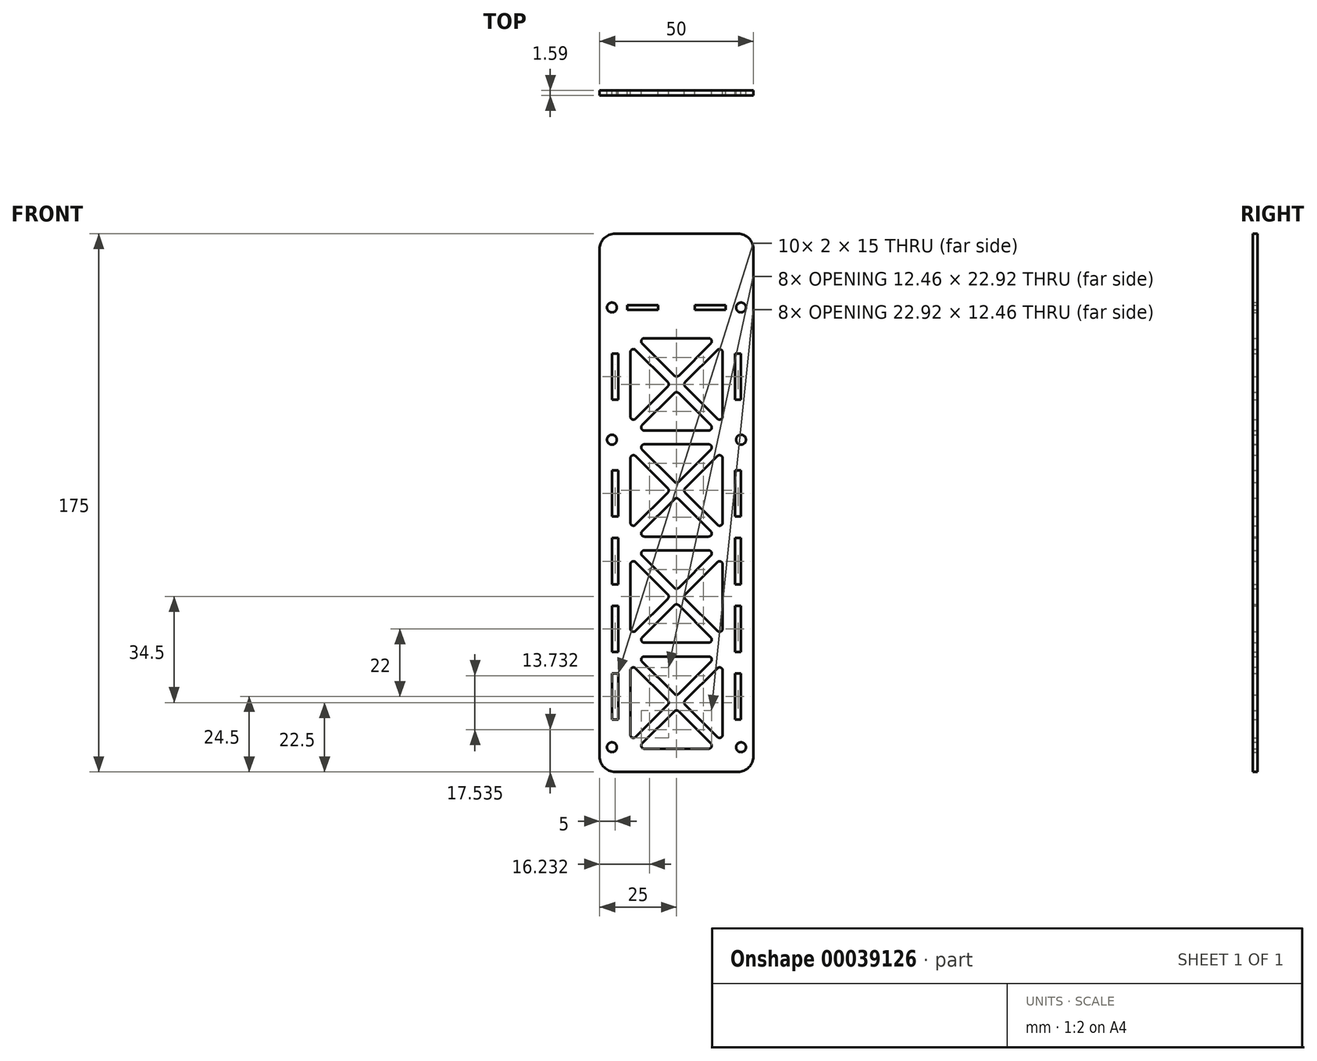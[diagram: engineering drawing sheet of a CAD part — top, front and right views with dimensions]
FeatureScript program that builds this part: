
annotation { "Feature Type Name" : "Feature", "Feature Type Description" : "" }
export const myFeature = defineFeature(function(context is Context, id is Id, definition is map)
    precondition{}
    {
        {
            var Q0;
            Q0=qCreatedBy(makeId("Front.planeOp"),FACE);
            var sketch = newSketch(context, id + "F0", { "sketchPlane" : qUnion([Q0])});
            skArc(sketch, "E0", {"start": v(15, -54.54) * mm, "mid": v(14.38, -53.61) * mm, "end": v(13.3, -53.83) * mm});
            skLineSegment(sketch, "E1", {"start": v(15, -75.46) * mm, "end": v(15, -54.54) * mm});
            skArc(sketch, "E2", {"start": v(13.3, -76.17) * mm, "mid": v(14.38, -76.39) * mm, "end": v(15, -75.46) * mm});
            skLineSegment(sketch, "E3", {"start": v(2.83, -65.7) * mm, "end": v(13.3, -76.17) * mm});
            skArc(sketch, "E4", {"start": v(2.83, -64.3) * mm, "mid": v(2.54, -65) * mm, "end": v(2.83, -65.7) * mm});
            skLineSegment(sketch, "E5", {"start": v(13.3, -53.83) * mm, "end": v(2.83, -64.3) * mm});
            skArc(sketch, "E6", {"start": v(-13.3, -53.83) * mm, "mid": v(-14.38, -53.61) * mm, "end": v(-15, -54.54) * mm});
            skLineSegment(sketch, "E7", {"start": v(-2.83, -64.3) * mm, "end": v(-13.3, -53.83) * mm});
            skArc(sketch, "E8", {"start": v(-2.83, -65.7) * mm, "mid": v(-2.54, -65) * mm, "end": v(-2.83, -64.3) * mm});
            skLineSegment(sketch, "E9", {"start": v(-13.3, -76.17) * mm, "end": v(-2.83, -65.7) * mm});
            skArc(sketch, "E10", {"start": v(-15, -75.46) * mm, "mid": v(-14.38, -76.39) * mm, "end": v(-13.3, -76.17) * mm});
            skLineSegment(sketch, "E11", {"start": v(-15, -54.54) * mm, "end": v(-15, -75.46) * mm});
            skArc(sketch, "E12", {"start": v(15, -20.04) * mm, "mid": v(14.38, -19.11) * mm, "end": v(13.3, -19.33) * mm});
            skLineSegment(sketch, "E13", {"start": v(15, -40.96) * mm, "end": v(15, -20.04) * mm});
            skArc(sketch, "E14", {"start": v(13.3, -41.67) * mm, "mid": v(14.38, -41.89) * mm, "end": v(15, -40.96) * mm});
            skLineSegment(sketch, "E15", {"start": v(2.83, -31.2) * mm, "end": v(13.3, -41.67) * mm});
            skArc(sketch, "E16", {"start": v(2.83, -29.8) * mm, "mid": v(2.54, -30.5) * mm, "end": v(2.83, -31.2) * mm});
            skLineSegment(sketch, "E17", {"start": v(13.3, -19.33) * mm, "end": v(2.83, -29.8) * mm});
            skArc(sketch, "E18", {"start": v(-13.3, -19.33) * mm, "mid": v(-14.38, -19.11) * mm, "end": v(-15, -20.04) * mm});
            skLineSegment(sketch, "E19", {"start": v(-2.83, -29.8) * mm, "end": v(-13.3, -19.33) * mm});
            skArc(sketch, "E20", {"start": v(-2.83, -31.2) * mm, "mid": v(-2.54, -30.5) * mm, "end": v(-2.83, -29.8) * mm});
            skLineSegment(sketch, "E21", {"start": v(-13.3, -41.67) * mm, "end": v(-2.83, -31.2) * mm});
            skArc(sketch, "E22", {"start": v(-15, -40.96) * mm, "mid": v(-14.38, -41.89) * mm, "end": v(-13.3, -41.67) * mm});
            skLineSegment(sketch, "E23", {"start": v(-15, -20.04) * mm, "end": v(-15, -40.96) * mm});
            skArc(sketch, "E24", {"start": v(15, 14.46) * mm, "mid": v(14.38, 15.39) * mm, "end": v(13.3, 15.17) * mm});
            skLineSegment(sketch, "E25", {"start": v(15, -6.46) * mm, "end": v(15, 14.46) * mm});
            skArc(sketch, "E26", {"start": v(13.3, -7.17) * mm, "mid": v(14.38, -7.39) * mm, "end": v(15, -6.46) * mm});
            skLineSegment(sketch, "E27", {"start": v(2.83, 3.3) * mm, "end": v(13.3, -7.17) * mm});
            skArc(sketch, "E28", {"start": v(2.83, 4.7) * mm, "mid": v(2.54, 4) * mm, "end": v(2.83, 3.3) * mm});
            skLineSegment(sketch, "E29", {"start": v(13.3, 15.17) * mm, "end": v(2.83, 4.7) * mm});
            skArc(sketch, "E30", {"start": v(-13.3, 15.17) * mm, "mid": v(-14.38, 15.39) * mm, "end": v(-15, 14.46) * mm});
            skLineSegment(sketch, "E31", {"start": v(-2.83, 4.7) * mm, "end": v(-13.3, 15.17) * mm});
            skArc(sketch, "E32", {"start": v(-2.83, 3.3) * mm, "mid": v(-2.54, 4) * mm, "end": v(-2.83, 4.7) * mm});
            skLineSegment(sketch, "E33", {"start": v(-13.3, -7.17) * mm, "end": v(-2.83, 3.3) * mm});
            skArc(sketch, "E34", {"start": v(-15, -6.46) * mm, "mid": v(-14.38, -7.39) * mm, "end": v(-13.3, -7.17) * mm});
            skLineSegment(sketch, "E35", {"start": v(-15, 14.46) * mm, "end": v(-15, -6.46) * mm});
            skArc(sketch, "E36", {"start": v(15, 48.96) * mm, "mid": v(14.38, 49.89) * mm, "end": v(13.3, 49.67) * mm});
            skLineSegment(sketch, "E37", {"start": v(15, 28.04) * mm, "end": v(15, 48.96) * mm});
            skArc(sketch, "E38", {"start": v(13.3, 27.33) * mm, "mid": v(14.38, 27.11) * mm, "end": v(15, 28.04) * mm});
            skLineSegment(sketch, "E39", {"start": v(2.83, 37.8) * mm, "end": v(13.3, 27.33) * mm});
            skArc(sketch, "E40", {"start": v(2.83, 39.2) * mm, "mid": v(2.54, 38.5) * mm, "end": v(2.83, 37.8) * mm});
            skLineSegment(sketch, "E41", {"start": v(13.3, 49.67) * mm, "end": v(2.83, 39.2) * mm});
            skArc(sketch, "E42", {"start": v(-13.3, 49.67) * mm, "mid": v(-14.38, 49.89) * mm, "end": v(-15, 48.96) * mm});
            skLineSegment(sketch, "E43", {"start": v(-2.83, 39.2) * mm, "end": v(-13.3, 49.67) * mm});
            skArc(sketch, "E44", {"start": v(-2.83, 37.8) * mm, "mid": v(-2.54, 38.5) * mm, "end": v(-2.83, 39.2) * mm});
            skLineSegment(sketch, "E45", {"start": v(-13.3, 27.33) * mm, "end": v(-2.83, 37.8) * mm});
            skArc(sketch, "E46", {"start": v(-15, 28.04) * mm, "mid": v(-14.38, 27.11) * mm, "end": v(-13.3, 27.33) * mm});
            skLineSegment(sketch, "E47", {"start": v(-15, 48.96) * mm, "end": v(-15, 28.04) * mm});
            skLineSegment(sketch, "E48", {"start": v(21, 10.5) * mm, "end": v(19, 10.5) * mm});
            skLineSegment(sketch, "E49", {"start": v(21, -4.5) * mm, "end": v(21, 10.5) * mm});
            skLineSegment(sketch, "E50", {"start": v(19, -4.5) * mm, "end": v(21, -4.5) * mm});
            skLineSegment(sketch, "E51", {"start": v(19, 10.5) * mm, "end": v(19, -4.5) * mm});
            skLineSegment(sketch, "E52", {"start": v(21, -33.5) * mm, "end": v(19, -33.5) * mm});
            skLineSegment(sketch, "E53", {"start": v(21, -48.5) * mm, "end": v(21, -33.5) * mm});
            skLineSegment(sketch, "E54", {"start": v(19, -48.5) * mm, "end": v(21, -48.5) * mm});
            skLineSegment(sketch, "E55", {"start": v(19, -33.5) * mm, "end": v(19, -48.5) * mm});
            skLineSegment(sketch, "E56", {"start": v(-21, -55.5) * mm, "end": v(-21, -70.5) * mm});
            skLineSegment(sketch, "E57", {"start": v(-19, -55.5) * mm, "end": v(-21, -55.5) * mm});
            skLineSegment(sketch, "E58", {"start": v(-19, -70.5) * mm, "end": v(-19, -55.5) * mm});
            skLineSegment(sketch, "E59", {"start": v(-21, -70.5) * mm, "end": v(-19, -70.5) * mm});
            skLineSegment(sketch, "E60", {"start": v(-21, -11.5) * mm, "end": v(-21, -26.5) * mm});
            skLineSegment(sketch, "E61", {"start": v(-19, -11.5) * mm, "end": v(-21, -11.5) * mm});
            skLineSegment(sketch, "E62", {"start": v(-19, -26.5) * mm, "end": v(-19, -11.5) * mm});
            skLineSegment(sketch, "E63", {"start": v(-21, -26.5) * mm, "end": v(-19, -26.5) * mm});
            skLineSegment(sketch, "E64", {"start": v(-21, 48.5) * mm, "end": v(-21, 33.5) * mm});
            skLineSegment(sketch, "E65", {"start": v(-19, 48.5) * mm, "end": v(-21, 48.5) * mm});
            skLineSegment(sketch, "E66", {"start": v(-19, 33.5) * mm, "end": v(-19, 48.5) * mm});
            skLineSegment(sketch, "E67", {"start": v(-21, 33.5) * mm, "end": v(-19, 33.5) * mm});
            skLineSegment(sketch, "E68", {"start": v(-16, 64.25) * mm, "end": v(-16, 62.75) * mm});
            skLineSegment(sketch, "E69", {"start": v(-6, 64.25) * mm, "end": v(-16, 64.25) * mm});
            skLineSegment(sketch, "E70", {"start": v(-6, 62.75) * mm, "end": v(-6, 64.25) * mm});
            skLineSegment(sketch, "E71", {"start": v(-16, 62.75) * mm, "end": v(-6, 62.75) * mm});
            skArc(sketch, "E72", {"start": v(25, 82.5) * mm, "mid": v(23.54, 86.04) * mm, "end": v(20, 87.5) * mm});
            skLineSegment(sketch, "E73", {"start": v(20, 87.5) * mm, "end": v(-20, 87.5) * mm});
            skArc(sketch, "E74", {"start": v(-20, 87.5) * mm, "mid": v(-23.54, 86.04) * mm, "end": v(-25, 82.5) * mm});
            skLineSegment(sketch, "E75", {"start": v(-25, 82.5) * mm, "end": v(-25, -82.5) * mm});
            skArc(sketch, "E76", {"start": v(-25, -82.5) * mm, "mid": v(-23.54, -86.04) * mm, "end": v(-20, -87.5) * mm});
            skLineSegment(sketch, "E77", {"start": v(-20, -87.5) * mm, "end": v(20, -87.5) * mm});
            skArc(sketch, "E78", {"start": v(20, -87.5) * mm, "mid": v(23.54, -86.04) * mm, "end": v(25, -82.5) * mm});
            skLineSegment(sketch, "E79", {"start": v(25, -82.5) * mm, "end": v(25, 82.5) * mm});
            skCircle(sketch, "E80", {"center": v(-21, 63.5) * mm, "radius": 1.6 * mm});
            skCircle(sketch, "E81", {"center": v(-21, 20.5) * mm, "radius": 1.6 * mm});
            skCircle(sketch, "E82", {"center": v(-21, -79.5) * mm, "radius": 1.6 * mm});
            skCircle(sketch, "E83", {"center": v(21, -79.5) * mm, "radius": 1.6 * mm});
            skCircle(sketch, "E84", {"center": v(21, 20.5) * mm, "radius": 1.6 * mm});
            skCircle(sketch, "E85", {"center": v(21, 63.5) * mm, "radius": 1.6 * mm});
            skLineSegment(sketch, "E86", {"start": v(16, 62.75) * mm, "end": v(16, 64.25) * mm});
            skLineSegment(sketch, "E87", {"start": v(6, 62.75) * mm, "end": v(16, 62.75) * mm});
            skLineSegment(sketch, "E88", {"start": v(6, 64.25) * mm, "end": v(6, 62.75) * mm});
            skLineSegment(sketch, "E89", {"start": v(16, 64.25) * mm, "end": v(6, 64.25) * mm});
            skLineSegment(sketch, "E90", {"start": v(-21, 10.5) * mm, "end": v(-21, -4.5) * mm});
            skLineSegment(sketch, "E91", {"start": v(-19, 10.5) * mm, "end": v(-21, 10.5) * mm});
            skLineSegment(sketch, "E92", {"start": v(-19, -4.5) * mm, "end": v(-19, 10.5) * mm});
            skLineSegment(sketch, "E93", {"start": v(-21, -4.5) * mm, "end": v(-19, -4.5) * mm});
            skLineSegment(sketch, "E94", {"start": v(-21, -33.5) * mm, "end": v(-21, -48.5) * mm});
            skLineSegment(sketch, "E95", {"start": v(-19, -33.5) * mm, "end": v(-21, -33.5) * mm});
            skLineSegment(sketch, "E96", {"start": v(-19, -48.5) * mm, "end": v(-19, -33.5) * mm});
            skLineSegment(sketch, "E97", {"start": v(-21, -48.5) * mm, "end": v(-19, -48.5) * mm});
            skLineSegment(sketch, "E98", {"start": v(21, -55.5) * mm, "end": v(19, -55.5) * mm});
            skLineSegment(sketch, "E99", {"start": v(21, -70.5) * mm, "end": v(21, -55.5) * mm});
            skLineSegment(sketch, "E100", {"start": v(19, -70.5) * mm, "end": v(21, -70.5) * mm});
            skLineSegment(sketch, "E101", {"start": v(19, -55.5) * mm, "end": v(19, -70.5) * mm});
            skLineSegment(sketch, "E102", {"start": v(21, -11.5) * mm, "end": v(19, -11.5) * mm});
            skLineSegment(sketch, "E103", {"start": v(21, -26.5) * mm, "end": v(21, -11.5) * mm});
            skLineSegment(sketch, "E104", {"start": v(19, -26.5) * mm, "end": v(21, -26.5) * mm});
            skLineSegment(sketch, "E105", {"start": v(19, -11.5) * mm, "end": v(19, -26.5) * mm});
            skLineSegment(sketch, "E106", {"start": v(21, 33.5) * mm, "end": v(21, 48.5) * mm});
            skLineSegment(sketch, "E107", {"start": v(19, 33.5) * mm, "end": v(21, 33.5) * mm});
            skLineSegment(sketch, "E108", {"start": v(19, 48.5) * mm, "end": v(19, 33.5) * mm});
            skLineSegment(sketch, "E109", {"start": v(21, 48.5) * mm, "end": v(19, 48.5) * mm});
            skArc(sketch, "E110", {"start": v(0.7, 35.67) * mm, "mid": v(0, 35.96) * mm, "end": v(-0.7, 35.67) * mm});
            skLineSegment(sketch, "E111", {"start": v(11.17, 25.2) * mm, "end": v(0.7, 35.67) * mm});
            skArc(sketch, "E112", {"start": v(10.46, 23.5) * mm, "mid": v(11.39, 24.12) * mm, "end": v(11.17, 25.2) * mm});
            skLineSegment(sketch, "E113", {"start": v(-10.46, 23.5) * mm, "end": v(10.46, 23.5) * mm});
            skArc(sketch, "E114", {"start": v(-11.17, 25.2) * mm, "mid": v(-11.39, 24.12) * mm, "end": v(-10.46, 23.5) * mm});
            skLineSegment(sketch, "E115", {"start": v(-0.7, 35.67) * mm, "end": v(-11.17, 25.2) * mm});
            skArc(sketch, "E116", {"start": v(-0.7, 41.33) * mm, "mid": v(0, 41.04) * mm, "end": v(0.7, 41.33) * mm});
            skLineSegment(sketch, "E117", {"start": v(-11.17, 51.8) * mm, "end": v(-0.7, 41.33) * mm});
            skArc(sketch, "E118", {"start": v(-10.46, 53.5) * mm, "mid": v(-11.39, 52.88) * mm, "end": v(-11.17, 51.8) * mm});
            skLineSegment(sketch, "E119", {"start": v(10.46, 53.5) * mm, "end": v(-10.46, 53.5) * mm});
            skArc(sketch, "E120", {"start": v(11.17, 51.8) * mm, "mid": v(11.39, 52.88) * mm, "end": v(10.46, 53.5) * mm});
            skLineSegment(sketch, "E121", {"start": v(0.7, 41.33) * mm, "end": v(11.17, 51.8) * mm});
            skArc(sketch, "E122", {"start": v(0.7, 1.17) * mm, "mid": v(0, 1.46) * mm, "end": v(-0.7, 1.17) * mm});
            skLineSegment(sketch, "E123", {"start": v(11.17, -9.3) * mm, "end": v(0.7, 1.17) * mm});
            skArc(sketch, "E124", {"start": v(10.46, -11) * mm, "mid": v(11.39, -10.38) * mm, "end": v(11.17, -9.3) * mm});
            skLineSegment(sketch, "E125", {"start": v(-10.46, -11) * mm, "end": v(10.46, -11) * mm});
            skArc(sketch, "E126", {"start": v(-11.17, -9.3) * mm, "mid": v(-11.39, -10.38) * mm, "end": v(-10.46, -11) * mm});
            skLineSegment(sketch, "E127", {"start": v(-0.7, 1.17) * mm, "end": v(-11.17, -9.3) * mm});
            skArc(sketch, "E128", {"start": v(-0.7, 6.83) * mm, "mid": v(0, 6.54) * mm, "end": v(0.7, 6.83) * mm});
            skLineSegment(sketch, "E129", {"start": v(-11.17, 17.3) * mm, "end": v(-0.7, 6.83) * mm});
            skArc(sketch, "E130", {"start": v(-10.46, 19) * mm, "mid": v(-11.39, 18.38) * mm, "end": v(-11.17, 17.3) * mm});
            skLineSegment(sketch, "E131", {"start": v(10.46, 19) * mm, "end": v(-10.46, 19) * mm});
            skArc(sketch, "E132", {"start": v(11.17, 17.3) * mm, "mid": v(11.39, 18.38) * mm, "end": v(10.46, 19) * mm});
            skLineSegment(sketch, "E133", {"start": v(0.7, 6.83) * mm, "end": v(11.17, 17.3) * mm});
            skArc(sketch, "E134", {"start": v(0.7, -33.33) * mm, "mid": v(0, -33.04) * mm, "end": v(-0.7, -33.33) * mm});
            skLineSegment(sketch, "E135", {"start": v(11.17, -43.8) * mm, "end": v(0.7, -33.33) * mm});
            skArc(sketch, "E136", {"start": v(10.46, -45.5) * mm, "mid": v(11.39, -44.88) * mm, "end": v(11.17, -43.8) * mm});
            skLineSegment(sketch, "E137", {"start": v(-10.46, -45.5) * mm, "end": v(10.46, -45.5) * mm});
            skArc(sketch, "E138", {"start": v(-11.17, -43.8) * mm, "mid": v(-11.39, -44.88) * mm, "end": v(-10.46, -45.5) * mm});
            skLineSegment(sketch, "E139", {"start": v(-0.7, -33.33) * mm, "end": v(-11.17, -43.8) * mm});
            skArc(sketch, "E140", {"start": v(-0.7, -27.67) * mm, "mid": v(0, -27.96) * mm, "end": v(0.7, -27.67) * mm});
            skLineSegment(sketch, "E141", {"start": v(-11.17, -17.2) * mm, "end": v(-0.7, -27.67) * mm});
            skArc(sketch, "E142", {"start": v(-10.46, -15.5) * mm, "mid": v(-11.39, -16.12) * mm, "end": v(-11.17, -17.2) * mm});
            skLineSegment(sketch, "E143", {"start": v(10.46, -15.5) * mm, "end": v(-10.46, -15.5) * mm});
            skArc(sketch, "E144", {"start": v(11.17, -17.2) * mm, "mid": v(11.39, -16.12) * mm, "end": v(10.46, -15.5) * mm});
            skLineSegment(sketch, "E145", {"start": v(0.7, -27.67) * mm, "end": v(11.17, -17.2) * mm});
            skArc(sketch, "E146", {"start": v(0.7, -67.83) * mm, "mid": v(0, -67.54) * mm, "end": v(-0.7, -67.83) * mm});
            skLineSegment(sketch, "E147", {"start": v(11.17, -78.3) * mm, "end": v(0.7, -67.83) * mm});
            skArc(sketch, "E148", {"start": v(10.46, -80) * mm, "mid": v(11.39, -79.38) * mm, "end": v(11.17, -78.3) * mm});
            skLineSegment(sketch, "E149", {"start": v(-10.46, -80) * mm, "end": v(10.46, -80) * mm});
            skArc(sketch, "E150", {"start": v(-11.17, -78.3) * mm, "mid": v(-11.39, -79.38) * mm, "end": v(-10.46, -80) * mm});
            skLineSegment(sketch, "E151", {"start": v(-0.7, -67.83) * mm, "end": v(-11.17, -78.3) * mm});
            skArc(sketch, "E152", {"start": v(-0.7, -62.17) * mm, "mid": v(0, -62.46) * mm, "end": v(0.7, -62.17) * mm});
            skLineSegment(sketch, "E153", {"start": v(-11.17, -51.7) * mm, "end": v(-0.7, -62.17) * mm});
            skArc(sketch, "E154", {"start": v(-10.46, -50) * mm, "mid": v(-11.39, -50.62) * mm, "end": v(-11.17, -51.7) * mm});
            skLineSegment(sketch, "E155", {"start": v(10.46, -50) * mm, "end": v(-10.46, -50) * mm});
            skArc(sketch, "E156", {"start": v(11.17, -51.7) * mm, "mid": v(11.39, -50.62) * mm, "end": v(10.46, -50) * mm});
            skLineSegment(sketch, "E157", {"start": v(0.7, -62.17) * mm, "end": v(11.17, -51.7) * mm});
            skSolve(sketch);
        }
        {
            var Q0;
            Q0 = qSketchRegion(id + "F0", true);
            extrude(context, id + "F1", {"entities" : qUnion([Q0]), "depth" : 1.59 * mm});
        }
    });
